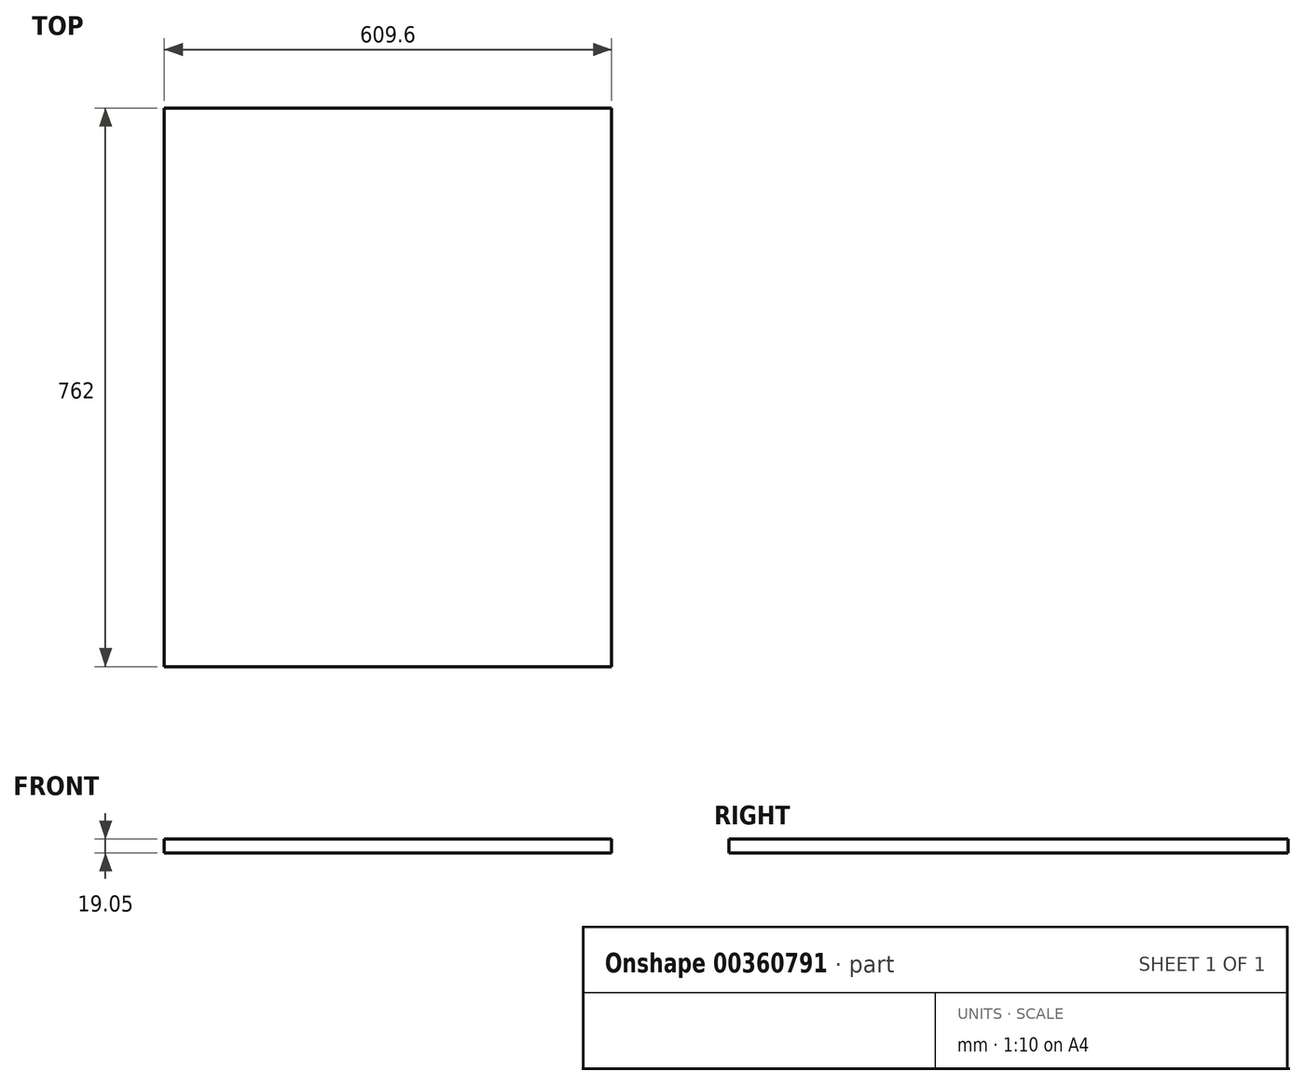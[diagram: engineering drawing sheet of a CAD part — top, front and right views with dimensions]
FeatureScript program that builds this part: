
annotation { "Feature Type Name" : "Feature", "Feature Type Description" : "" }
export const myFeature = defineFeature(function(context is Context, id is Id, definition is map)
    precondition{}
    {
        {
            var Q0;
            Q0=qCreatedBy(makeId("Top.planeOp"),FACE);
            var sketch = newSketch(context, id + "F0", { "sketchPlane" : qUnion([Q0])});
            skLineSegment(sketch, "E0.bottom", {"start": v(0, 0) * mm, "end": v(609.6, 0) * mm});
            skLineSegment(sketch, "E0.top", {"start": v(0, -762) * mm, "end": v(609.6, -762) * mm});
            skLineSegment(sketch, "E0.left", {"start": v(0, 0) * mm, "end": v(0, -762) * mm});
            skLineSegment(sketch, "E0.right", {"start": v(609.6, 0) * mm, "end": v(609.6, -762) * mm});
            skSolve(sketch);
        }
        {
            var Q0;
            Q0 = qSketchRegion(id + "F0", true);
            extrude(context, id + "F1", {"entities" : qUnion([Q0]), "depth" : 19.05 * mm});
        }
    });
